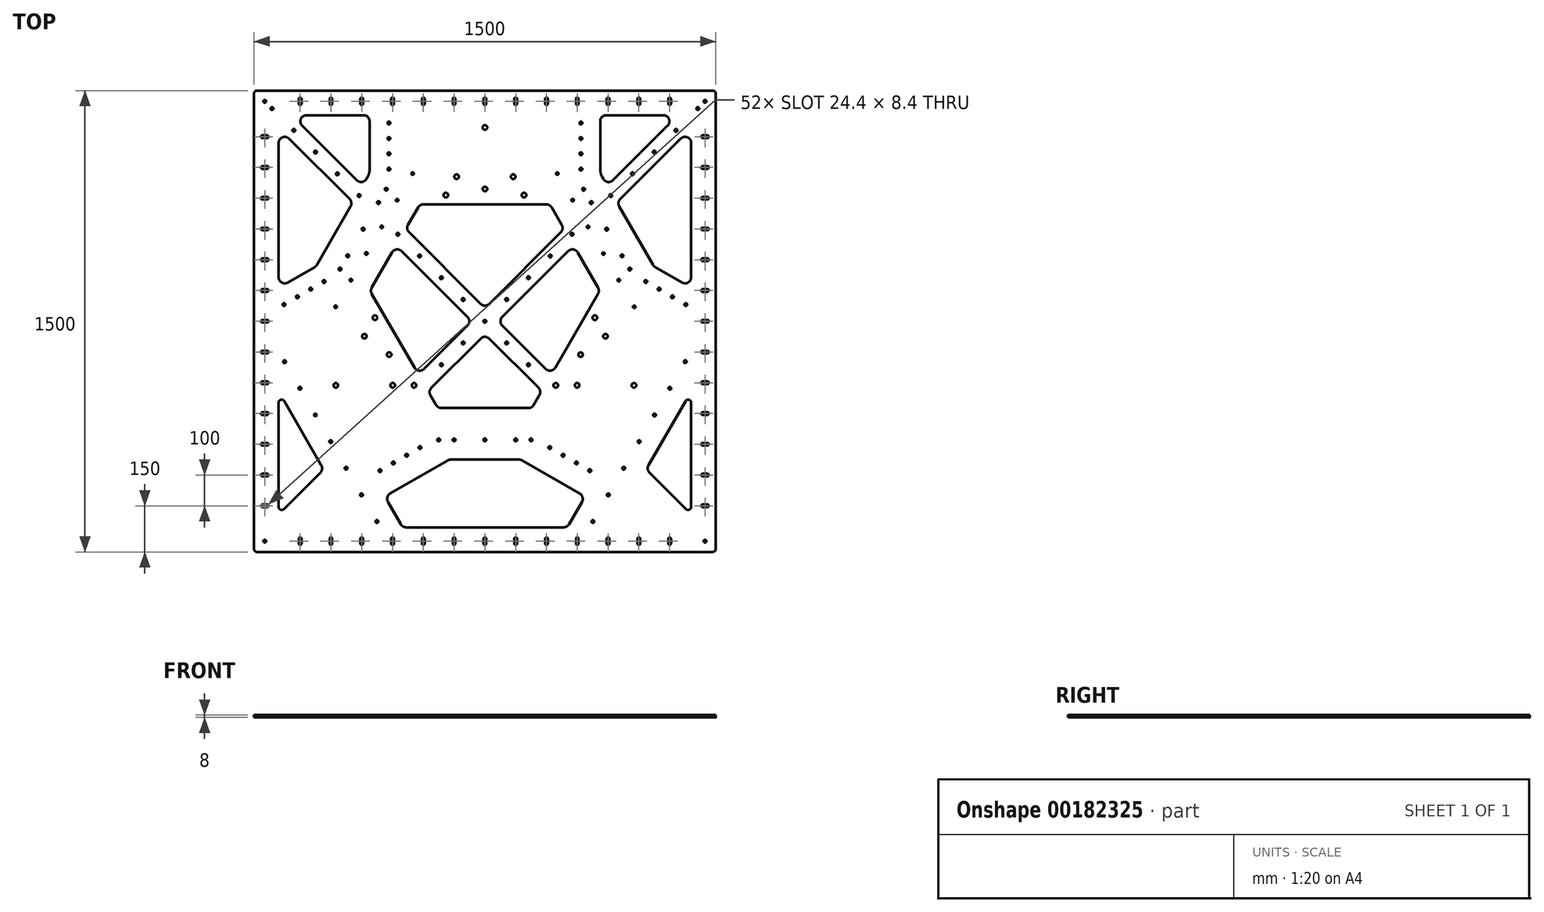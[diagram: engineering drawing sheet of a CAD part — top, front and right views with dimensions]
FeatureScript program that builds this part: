
annotation { "Feature Type Name" : "Feature", "Feature Type Description" : "" }
export const myFeature = defineFeature(function(context is Context, id is Id, definition is map)
    precondition{}
    {
        {
            var Q0;
            Q0=qCreatedBy(makeId("Top.planeOp"),FACE);
            var sketch = newSketch(context, id + "F0", { "sketchPlane" : qUnion([Q0])});
            skLineSegment(sketch, "E0.bottom", {"start": v(750, -750) * mm, "end": v(-750, -750) * mm});
            skLineSegment(sketch, "E0.top", {"start": v(750, 750) * mm, "end": v(-750, 750) * mm});
            skLineSegment(sketch, "E0.left", {"start": v(750, -750) * mm, "end": v(750, 750) * mm});
            skLineSegment(sketch, "E0.right", {"start": v(-750, -750) * mm, "end": v(-750, 750) * mm});
            skPoint(sketch, "E0.middle", {"position": v(0, 0) * mm});
            skSolve(sketch);
        }
        {
            var Q0;
            Q0=qSketchRegion(id+"F0",true);
            extrude(context, id + "F1", {"entities" : qUnion([Q0]), "depth" : 8 * mm});
        }
        {
            var Q0;
            Q0=makeQuery(id+"F1.opExtrude","CAP_FACE",FACE,{"disambiguationData":[OSD([sQuery(id+"F0.wireOp",EDGE,"E0.bottom"),sQuery(id+"F0.wireOp",EDGE,"E0.top"),sQuery(id+"F0.wireOp",EDGE,"E0.left"),sQuery(id+"F0.wireOp",EDGE,"E0.right")])],"isStart":false});
            var sketch = newSketch(context, id + "F2", { "sketchPlane" : qUnion([Q0])});
            skLineSegment(sketch, "E1", {"start": v(0, -750) * mm, "end": v(0, 750) * mm, "construction": true});
            skCircle(sketch, "E2", {"center": v(0, 71) * mm, "radius": 559 * mm, "construction": true});
            skCircle(sketch, "E3", {"center": v(0, 630) * mm, "radius": 7.5 * mm});
            skLineSegment(sketch, "E4", {"start": v(0, 71) * mm, "end": v(-275.24, -87.91) * mm, "construction": true});
            skLineSegment(sketch, "E5", {"start": v(0, 71) * mm, "end": v(329.13, -119.03) * mm, "construction": true});
            skCircle(sketch, "E6.MirrorC", {"center": v(-484.1, -208.5) * mm, "radius": 7.5 * mm});
            skCircle(sketch, "E7.MirrorC", {"center": v(484.1, -208.5) * mm, "radius": 7.5 * mm});
            skCircle(sketch, "E8", {"center": v(0, 71) * mm, "radius": 362 * mm, "construction": true});
            skCircle(sketch, "E9", {"center": v(0, 71) * mm, "radius": 409.5 * mm, "construction": true});
            skCircle(sketch, "E10", {"center": v(-92, 470.03) * mm, "radius": 7.5 * mm});
            skCircle(sketch, "E11.MirrorC", {"center": v(92, 470.03) * mm, "radius": 7.5 * mm});
            skCircle(sketch, "E12", {"center": v(-127, 410) * mm, "radius": 7.5 * mm});
            skCircle(sketch, "E13.MirrorC", {"center": v(127, 410) * mm, "radius": 7.5 * mm});
            skCircle(sketch, "E14.MirrorC", {"center": v(-230.07, -208.48) * mm, "radius": 7.5 * mm});
            skCircle(sketch, "E15.MirrorC", {"center": v(-357.07, 11.49) * mm, "radius": 7.5 * mm});
            skCircle(sketch, "E16.MirrorC", {"center": v(-299.57, -208.2) * mm, "radius": 7.5 * mm});
            skCircle(sketch, "E17.MirrorC", {"center": v(-391.57, -48.84) * mm, "radius": 7.5 * mm});
            skCircle(sketch, "E18.MirrorC", {"center": v(391.57, -48.84) * mm, "radius": 7.5 * mm});
            skCircle(sketch, "E19.MirrorC", {"center": v(299.57, -208.2) * mm, "radius": 7.5 * mm});
            skCircle(sketch, "E20.MirrorC", {"center": v(230.07, -208.48) * mm, "radius": 7.5 * mm});
            skCircle(sketch, "E21.MirrorC", {"center": v(357.07, 11.49) * mm, "radius": 7.5 * mm});
            skPoint(sketch, "E22.middle", {"position": v(0, 435.08) * mm});
            skCircle(sketch, "E23", {"center": v(0, 430) * mm, "radius": 7.5 * mm});
            skCircle(sketch, "E24.MirrorC", {"center": v(310.9, -108.5) * mm, "radius": 7.5 * mm});
            skCircle(sketch, "E25.MirrorC", {"center": v(-310.9, -108.5) * mm, "radius": 7.5 * mm});
            skSolve(sketch);
        }
        {
            var Q0;
            Q0=qSketchRegion(id+"F2",true);
            extrude(context, id + "F3", {"entities" : qUnion([Q0]), "operationType" : NewBodyOperationType.REMOVE, "endBound" : BoundingType.THROUGH_ALL, "oppositeDirection" : true, "depth" : 25 * mm});
        }
        {
            var Q0;
            Q0=makeQuery(id+"F1.opExtrude","CAP_FACE",FACE,{"disambiguationData":[OSD([sQuery(id+"F0.wireOp",EDGE,"E0.bottom"),sQuery(id+"F0.wireOp",EDGE,"E0.top"),sQuery(id+"F0.wireOp",EDGE,"E0.left"),sQuery(id+"F0.wireOp",EDGE,"E0.right")])],"isStart":false});
            var sketch = newSketch(context, id + "F4", { "sketchPlane" : qUnion([Q0])});
            skLineSegment(sketch, "E26", {"start": v(0, 750) * mm, "end": v(0, -750) * mm, "construction": true});
            skLineSegment(sketch, "E27", {"start": v(-627.57, 670) * mm, "end": v(-374.68, 670) * mm});
            skLineSegment(sketch, "E28", {"start": v(-397.7, 440.12) * mm, "end": v(-627.57, 670) * mm});
            skLineSegment(sketch, "E29.MirrorCS", {"start": v(627.57, 670) * mm, "end": v(374.68, 670) * mm});
            skLineSegment(sketch, "E30.MirrorCS", {"start": v(397.7, 440.12) * mm, "end": v(627.57, 670) * mm});
            skLineSegment(sketch, "E31", {"start": v(-257.5, 299.93) * mm, "end": v(257.5, 299.93) * mm, "construction": true});
            skLineSegment(sketch, "E32", {"start": v(257.5, 299.93) * mm, "end": v(0, 42.43) * mm});
            skLineSegment(sketch, "E33.MirrorCS", {"start": v(-257.5, 299.93) * mm, "end": v(0, 42.43) * mm});
            skLineSegment(sketch, "E34", {"start": v(-399.35, 0) * mm, "end": v(437.87, 0) * mm, "construction": true});
            skLineSegment(sketch, "E35.MirrorCS", {"start": v(-257.5, -299.93) * mm, "end": v(0, -42.43) * mm});
            skLineSegment(sketch, "E36.MirrorCS", {"start": v(-257.5, -299.93) * mm, "end": v(257.5, -299.93) * mm, "construction": true});
            skLineSegment(sketch, "E37.MirrorCS", {"start": v(257.5, -299.93) * mm, "end": v(0, -42.43) * mm});
            skLineSegment(sketch, "E38", {"start": v(-215.67, -173.24) * mm, "end": v(-42.43, 0) * mm});
            skLineSegment(sketch, "E39.MirrorCS", {"start": v(-215.67, 173.24) * mm, "end": v(-42.43, 0) * mm});
            skLineSegment(sketch, "E40.MirrorCS", {"start": v(215.67, 173.24) * mm, "end": v(42.43, 0) * mm});
            skLineSegment(sketch, "E41.MirrorCS", {"start": v(215.67, -173.24) * mm, "end": v(42.43, 0) * mm});
            skLineSegment(sketch, "E42", {"start": v(750, 750) * mm, "end": v(-750, -750) * mm, "construction": true});
            skLineSegment(sketch, "E43", {"start": v(-750, 750) * mm, "end": v(750, -750) * mm, "construction": true});
            skLineSegment(sketch, "E44", {"start": v(-750, -707.57) * mm, "end": v(707.57, 750) * mm, "construction": true});
            skLineSegment(sketch, "E45", {"start": v(750, 707.57) * mm, "end": v(-707.57, -750) * mm, "construction": true});
            skLineSegment(sketch, "E46", {"start": v(-215.67, 173.24) * mm, "end": v(-315.69, 0) * mm, "construction": true});
            skLineSegment(sketch, "E47", {"start": v(-315.69, 0) * mm, "end": v(-215.67, -173.24) * mm});
            skLineSegment(sketch, "E48.MirrorCS", {"start": v(315.69, 0) * mm, "end": v(215.67, -173.24) * mm});
            skLineSegment(sketch, "E49.MirrorCS", {"start": v(215.67, 173.24) * mm, "end": v(315.69, 0) * mm, "construction": true});
            skLineSegment(sketch, "E50", {"start": v(670, 627.57) * mm, "end": v(428.76, 386.33) * mm});
            skLineSegment(sketch, "E51", {"start": v(670, 108.48) * mm, "end": v(670, 627.57) * mm});
            skLineSegment(sketch, "E52", {"start": v(-184.6, -227.04) * mm, "end": v(-257.5, -299.93) * mm});
            skLineSegment(sketch, "E53", {"start": v(-184.6, -227.04) * mm, "end": v(184.6, -227.04) * mm, "construction": true});
            skLineSegment(sketch, "E54", {"start": v(257.5, -299.93) * mm, "end": v(184.6, -227.04) * mm});
            skLineSegment(sketch, "E55", {"start": v(-670, -227.57) * mm, "end": v(-670, -627.57) * mm});
            skLineSegment(sketch, "E56", {"start": v(-670, -627.57) * mm, "end": v(-523.59, -481.16) * mm});
            skLineSegment(sketch, "E57", {"start": v(-523.59, -481.16) * mm, "end": v(-670, -227.57) * mm});
            skLineSegment(sketch, "E58.MirrorCS", {"start": v(523.59, -481.16) * mm, "end": v(670, -227.57) * mm});
            skLineSegment(sketch, "E59.MirrorCS", {"start": v(670, -627.57) * mm, "end": v(523.59, -481.16) * mm});
            skLineSegment(sketch, "E60.MirrorCS", {"start": v(670, -227.57) * mm, "end": v(670, -627.57) * mm});
            skLineSegment(sketch, "E61", {"start": v(0, -450) * mm, "end": v(-117.15, -450) * mm});
            skLineSegment(sketch, "E62", {"start": v(-117.15, -450) * mm, "end": v(-325, -570) * mm});
            skLineSegment(sketch, "E63", {"start": v(-325, -570) * mm, "end": v(0, -570) * mm, "construction": true});
            skLineSegment(sketch, "E64.MirrorCS", {"start": v(0, -450) * mm, "end": v(117.15, -450) * mm});
            skLineSegment(sketch, "E65.MirrorCS", {"start": v(325, -570) * mm, "end": v(0, -570) * mm, "construction": true});
            skLineSegment(sketch, "E66.MirrorCS", {"start": v(117.15, -450) * mm, "end": v(325, -570) * mm});
            skLineSegment(sketch, "E67.MirrorCS", {"start": v(-670, 108.48) * mm, "end": v(-670, 627.57) * mm});
            skLineSegment(sketch, "E68.MirrorCS", {"start": v(-670, 627.57) * mm, "end": v(-428.76, 386.33) * mm});
            skLineSegment(sketch, "E69", {"start": v(428.76, 386.33) * mm, "end": v(548.76, 178.48) * mm});
            skLineSegment(sketch, "E70", {"start": v(548.76, 178.48) * mm, "end": v(670, 108.48) * mm});
            skLineSegment(sketch, "E71.MirrorCS", {"start": v(-428.76, 386.33) * mm, "end": v(-548.76, 178.48) * mm});
            skLineSegment(sketch, "E72.MirrorCS", {"start": v(-548.76, 178.48) * mm, "end": v(-670, 108.48) * mm});
            skLineSegment(sketch, "E73", {"start": v(-184.6, -227.04) * mm, "end": v(-152.63, -282.43) * mm});
            skLineSegment(sketch, "E74", {"start": v(-152.63, -282.43) * mm, "end": v(0, -282.43) * mm});
            skLineSegment(sketch, "E75.MirrorCS", {"start": v(152.63, -282.43) * mm, "end": v(0, -282.43) * mm});
            skLineSegment(sketch, "E76.MirrorCS", {"start": v(184.6, -227.04) * mm, "end": v(152.63, -282.43) * mm});
            skLineSegment(sketch, "E77", {"start": v(-408.03, 159.94) * mm, "end": v(-88.62, -393.3) * mm, "construction": true});
            skLineSegment(sketch, "E78", {"start": v(-215.67, 173.24) * mm, "end": v(-288.56, 246.13) * mm});
            skLineSegment(sketch, "E79", {"start": v(-288.56, 246.13) * mm, "end": v(-373.18, 99.57) * mm});
            skLineSegment(sketch, "E80", {"start": v(-315.69, 0) * mm, "end": v(-373.18, 99.57) * mm});
            skLineSegment(sketch, "E81.MirrorCS", {"start": v(288.56, 246.13) * mm, "end": v(373.18, 99.57) * mm});
            skLineSegment(sketch, "E82.MirrorCS", {"start": v(315.69, 0) * mm, "end": v(373.18, 99.57) * mm});
            skLineSegment(sketch, "E83.MirrorCS", {"start": v(215.67, 173.24) * mm, "end": v(288.56, 246.13) * mm});
            skLineSegment(sketch, "E84", {"start": v(-257.5, 299.93) * mm, "end": v(-462.8, -55.67) * mm, "construction": true});
            skLineSegment(sketch, "E85", {"start": v(-257.5, 299.93) * mm, "end": v(-211.31, 379.93) * mm});
            skLineSegment(sketch, "E86", {"start": v(-211.31, 379.93) * mm, "end": v(0, 379.93) * mm});
            skLineSegment(sketch, "E87.MirrorCS", {"start": v(211.31, 379.93) * mm, "end": v(0, 379.93) * mm});
            skLineSegment(sketch, "E88.MirrorCS", {"start": v(257.5, 299.93) * mm, "end": v(211.31, 379.93) * mm});
            skLineSegment(sketch, "E89", {"start": v(-325, -570) * mm, "end": v(-267.26, -670) * mm});
            skLineSegment(sketch, "E90", {"start": v(-267.26, -670) * mm, "end": v(0, -670) * mm});
            skLineSegment(sketch, "E91.MirrorCS", {"start": v(267.26, -670) * mm, "end": v(0, -670) * mm});
            skLineSegment(sketch, "E92.MirrorCS", {"start": v(325, -570) * mm, "end": v(267.26, -670) * mm});
            skLineSegment(sketch, "E93", {"start": v(428.76, 386.33) * mm, "end": v(397.7, 440.12) * mm, "construction": true});
            skLineSegment(sketch, "E94", {"start": v(397.7, 440.12) * mm, "end": v(374.68, 480) * mm});
            skLineSegment(sketch, "E95", {"start": v(374.68, 480) * mm, "end": v(374.68, 670) * mm});
            skLineSegment(sketch, "E96.MirrorCS", {"start": v(-374.68, 480) * mm, "end": v(-374.68, 670) * mm});
            skLineSegment(sketch, "E97.MirrorCS", {"start": v(-397.7, 440.12) * mm, "end": v(-374.68, 480) * mm});
            skSolve(sketch);
        }
        {
            var Q0;
            Q0 = qSketchRegion(id + "F4", true);
            extrude(context, id + "F5", {"entities" : qUnion([Q0]), "operationType" : NewBodyOperationType.REMOVE, "endBound" : BoundingType.THROUGH_ALL, "oppositeDirection" : true, "depth" : 25 * mm});
        }
        {
            var Q0;
            Q0=makeQuery(id+"F1.opExtrude","CAP_FACE",FACE,{"disambiguationData":[OSD([sQuery(id+"F0.wireOp",EDGE,"E0.bottom"),sQuery(id+"F0.wireOp",EDGE,"E0.top"),sQuery(id+"F0.wireOp",EDGE,"E0.left"),sQuery(id+"F0.wireOp",EDGE,"E0.right")])],"isStart":false});
            var sketch = newSketch(context, id + "F6", { "sketchPlane" : qUnion([Q0])});
            skLineSegment(sketch, "E98", {"start": v(0, 750) * mm, "end": v(0, -750) * mm, "construction": true});
            skLineSegment(sketch, "E99.left", {"start": v(-595.8, 707) * mm, "end": v(-595.8, 723) * mm});
            skLineSegment(sketch, "E99.right", {"start": v(-604.2, 707) * mm, "end": v(-604.2, 723) * mm});
            skPoint(sketch, "E99.middle", {"position": v(-600, 715) * mm});
            skArc(sketch, "E100", {"start": v(-595.8, 723) * mm, "mid": v(-600, 727.2) * mm, "end": v(-604.2, 723) * mm});
            skArc(sketch, "E101", {"start": v(-604.2, 707) * mm, "mid": v(-600, 702.8) * mm, "end": v(-595.8, 707) * mm});
            skLineSegment(sketch, "E102", {"start": v(-604.2, 723) * mm, "end": v(-595.8, 723) * mm, "construction": true});
            skArc(sketch, "E103.1.0.0", {"start": v(-504.2, 707) * mm, "mid": v(-500, 702.8) * mm, "end": v(-495.8, 707) * mm});
            skLineSegment(sketch, "E103.1.0.1", {"start": v(-495.8, 707) * mm, "end": v(-495.8, 723) * mm});
            skArc(sketch, "E103.1.0.2", {"start": v(-495.8, 723) * mm, "mid": v(-500, 727.2) * mm, "end": v(-504.2, 723) * mm});
            skLineSegment(sketch, "E103.1.0.3", {"start": v(-504.2, 707) * mm, "end": v(-504.2, 723) * mm});
            skArc(sketch, "E103.2.0.0", {"start": v(-404.2, 707) * mm, "mid": v(-400, 702.8) * mm, "end": v(-395.8, 707) * mm});
            skLineSegment(sketch, "E103.2.0.1", {"start": v(-395.8, 707) * mm, "end": v(-395.8, 723) * mm});
            skArc(sketch, "E103.2.0.2", {"start": v(-395.8, 723) * mm, "mid": v(-400, 727.2) * mm, "end": v(-404.2, 723) * mm});
            skLineSegment(sketch, "E103.2.0.3", {"start": v(-404.2, 707) * mm, "end": v(-404.2, 723) * mm});
            skArc(sketch, "E103.3.0.0", {"start": v(-304.2, 707) * mm, "mid": v(-300, 702.8) * mm, "end": v(-295.8, 707) * mm});
            skLineSegment(sketch, "E103.3.0.1", {"start": v(-295.8, 707) * mm, "end": v(-295.8, 723) * mm});
            skArc(sketch, "E103.3.0.2", {"start": v(-295.8, 723) * mm, "mid": v(-300, 727.2) * mm, "end": v(-304.2, 723) * mm});
            skLineSegment(sketch, "E103.3.0.3", {"start": v(-304.2, 707) * mm, "end": v(-304.2, 723) * mm});
            skArc(sketch, "E103.4.0.0", {"start": v(-204.2, 707) * mm, "mid": v(-200, 702.8) * mm, "end": v(-195.8, 707) * mm});
            skLineSegment(sketch, "E103.4.0.1", {"start": v(-195.8, 707) * mm, "end": v(-195.8, 723) * mm});
            skArc(sketch, "E103.4.0.2", {"start": v(-195.8, 723) * mm, "mid": v(-200, 727.2) * mm, "end": v(-204.2, 723) * mm});
            skLineSegment(sketch, "E103.4.0.3", {"start": v(-204.2, 707) * mm, "end": v(-204.2, 723) * mm});
            skArc(sketch, "E103.5.0.0", {"start": v(-104.2, 707) * mm, "mid": v(-100, 702.8) * mm, "end": v(-95.8, 707) * mm});
            skLineSegment(sketch, "E103.5.0.1", {"start": v(-95.8, 707) * mm, "end": v(-95.8, 723) * mm});
            skArc(sketch, "E103.5.0.2", {"start": v(-95.8, 723) * mm, "mid": v(-100, 727.2) * mm, "end": v(-104.2, 723) * mm});
            skLineSegment(sketch, "E103.5.0.3", {"start": v(-104.2, 707) * mm, "end": v(-104.2, 723) * mm});
            skArc(sketch, "E103.6.0.0", {"start": v(-4.2, 707) * mm, "mid": v(0, 702.8) * mm, "end": v(4.2, 707) * mm});
            skLineSegment(sketch, "E103.6.0.1", {"start": v(4.2, 707) * mm, "end": v(4.2, 723) * mm});
            skArc(sketch, "E103.6.0.2", {"start": v(4.2, 723) * mm, "mid": v(0, 727.2) * mm, "end": v(-4.2, 723) * mm});
            skLineSegment(sketch, "E103.6.0.3", {"start": v(-4.2, 707) * mm, "end": v(-4.2, 723) * mm});
            skArc(sketch, "E103.7.0.0", {"start": v(95.8, 707) * mm, "mid": v(100, 702.8) * mm, "end": v(104.2, 707) * mm});
            skLineSegment(sketch, "E103.7.0.1", {"start": v(104.2, 707) * mm, "end": v(104.2, 723) * mm});
            skArc(sketch, "E103.7.0.2", {"start": v(104.2, 723) * mm, "mid": v(100, 727.2) * mm, "end": v(95.8, 723) * mm});
            skLineSegment(sketch, "E103.7.0.3", {"start": v(95.8, 707) * mm, "end": v(95.8, 723) * mm});
            skArc(sketch, "E103.8.0.0", {"start": v(195.8, 707) * mm, "mid": v(200, 702.8) * mm, "end": v(204.2, 707) * mm});
            skLineSegment(sketch, "E103.8.0.1", {"start": v(204.2, 707) * mm, "end": v(204.2, 723) * mm});
            skArc(sketch, "E103.8.0.2", {"start": v(204.2, 723) * mm, "mid": v(200, 727.2) * mm, "end": v(195.8, 723) * mm});
            skLineSegment(sketch, "E103.8.0.3", {"start": v(195.8, 707) * mm, "end": v(195.8, 723) * mm});
            skArc(sketch, "E103.9.0.0", {"start": v(295.8, 707) * mm, "mid": v(300, 702.8) * mm, "end": v(304.2, 707) * mm});
            skLineSegment(sketch, "E103.9.0.1", {"start": v(304.2, 707) * mm, "end": v(304.2, 723) * mm});
            skArc(sketch, "E103.9.0.2", {"start": v(304.2, 723) * mm, "mid": v(300, 727.2) * mm, "end": v(295.8, 723) * mm});
            skLineSegment(sketch, "E103.9.0.3", {"start": v(295.8, 707) * mm, "end": v(295.8, 723) * mm});
            skArc(sketch, "E103.10.0.0", {"start": v(395.8, 707) * mm, "mid": v(400, 702.8) * mm, "end": v(404.2, 707) * mm});
            skLineSegment(sketch, "E103.10.0.1", {"start": v(404.2, 707) * mm, "end": v(404.2, 723) * mm});
            skArc(sketch, "E103.10.0.2", {"start": v(404.2, 723) * mm, "mid": v(400, 727.2) * mm, "end": v(395.8, 723) * mm});
            skLineSegment(sketch, "E103.10.0.3", {"start": v(395.8, 707) * mm, "end": v(395.8, 723) * mm});
            skArc(sketch, "E103.11.0.0", {"start": v(495.8, 707) * mm, "mid": v(500, 702.8) * mm, "end": v(504.2, 707) * mm});
            skLineSegment(sketch, "E103.11.0.1", {"start": v(504.2, 707) * mm, "end": v(504.2, 723) * mm});
            skArc(sketch, "E103.11.0.2", {"start": v(504.2, 723) * mm, "mid": v(500, 727.2) * mm, "end": v(495.8, 723) * mm});
            skLineSegment(sketch, "E103.11.0.3", {"start": v(495.8, 707) * mm, "end": v(495.8, 723) * mm});
            skArc(sketch, "E103.12.0.0", {"start": v(595.8, 707) * mm, "mid": v(600, 702.8) * mm, "end": v(604.2, 707) * mm});
            skLineSegment(sketch, "E103.12.0.1", {"start": v(604.2, 707) * mm, "end": v(604.2, 723) * mm});
            skArc(sketch, "E103.12.0.2", {"start": v(604.2, 723) * mm, "mid": v(600, 727.2) * mm, "end": v(595.8, 723) * mm});
            skLineSegment(sketch, "E103.12.0.3", {"start": v(595.8, 707) * mm, "end": v(595.8, 723) * mm});
            skLineSegment(sketch, "E103.direction1", {"start": v(-604.2, 707) * mm, "end": v(-504.2, 707) * mm, "construction": true});
            skLineSegment(sketch, "E104", {"start": v(-750, 723) * mm, "end": v(750, 723) * mm, "construction": true});
            skLineSegment(sketch, "E105", {"start": v(-750, 0) * mm, "end": v(750, 0) * mm, "construction": true});
            skArc(sketch, "E106.MirrorCS", {"start": v(-295.8, -723) * mm, "mid": v(-300, -727.2) * mm, "end": v(-304.2, -723) * mm});
            skArc(sketch, "E107.MirrorCS", {"start": v(-495.8, -723) * mm, "mid": v(-500, -727.2) * mm, "end": v(-504.2, -723) * mm});
            skLineSegment(sketch, "E108.MirrorCS", {"start": v(304.2, -707) * mm, "end": v(304.2, -723) * mm});
            skLineSegment(sketch, "E109.MirrorCS", {"start": v(-495.8, -707) * mm, "end": v(-495.8, -723) * mm});
            skArc(sketch, "E110.MirrorCS", {"start": v(-504.2, -707) * mm, "mid": v(-500, -702.8) * mm, "end": v(-495.8, -707) * mm});
            skLineSegment(sketch, "E111.MirrorCS", {"start": v(-604.2, -723) * mm, "end": v(-595.8, -723) * mm, "construction": true});
            skArc(sketch, "E112.MirrorCS", {"start": v(-604.2, -707) * mm, "mid": v(-600, -702.8) * mm, "end": v(-595.8, -707) * mm});
            skArc(sketch, "E113.MirrorCS", {"start": v(-595.8, -723) * mm, "mid": v(-600, -727.2) * mm, "end": v(-604.2, -723) * mm});
            skLineSegment(sketch, "E114.MirrorCS", {"start": v(-604.2, -707) * mm, "end": v(-604.2, -723) * mm});
            skLineSegment(sketch, "E115.MirrorCS", {"start": v(-295.8, -707) * mm, "end": v(-295.8, -723) * mm});
            skLineSegment(sketch, "E116.MirrorCS", {"start": v(-595.8, -707) * mm, "end": v(-595.8, -723) * mm});
            skArc(sketch, "E117.MirrorCS", {"start": v(-304.2, -707) * mm, "mid": v(-300, -702.8) * mm, "end": v(-295.8, -707) * mm});
            skLineSegment(sketch, "E118.MirrorCS", {"start": v(-304.2, -707) * mm, "end": v(-304.2, -723) * mm});
            skArc(sketch, "E119.MirrorCS", {"start": v(295.8, -707) * mm, "mid": v(300, -702.8) * mm, "end": v(304.2, -707) * mm});
            skArc(sketch, "E120.MirrorCS", {"start": v(304.2, -723) * mm, "mid": v(300, -727.2) * mm, "end": v(295.8, -723) * mm});
            skLineSegment(sketch, "E121.MirrorCS", {"start": v(295.8, -707) * mm, "end": v(295.8, -723) * mm});
            skLineSegment(sketch, "E122.MirrorCS", {"start": v(-504.2, -707) * mm, "end": v(-504.2, -723) * mm});
            skArc(sketch, "E123.MirrorCS", {"start": v(-4.2, -707) * mm, "mid": v(0, -702.8) * mm, "end": v(4.2, -707) * mm});
            skArc(sketch, "E124.MirrorCS", {"start": v(104.2, -723) * mm, "mid": v(100, -727.2) * mm, "end": v(95.8, -723) * mm});
            skLineSegment(sketch, "E125.MirrorCS", {"start": v(-4.2, -707) * mm, "end": v(-4.2, -723) * mm});
            skArc(sketch, "E126.MirrorCS", {"start": v(4.2, -723) * mm, "mid": v(0, -727.2) * mm, "end": v(-4.2, -723) * mm});
            skLineSegment(sketch, "E127.MirrorCS", {"start": v(4.2, -707) * mm, "end": v(4.2, -723) * mm});
            skArc(sketch, "E128.MirrorCS", {"start": v(-195.8, -723) * mm, "mid": v(-200, -727.2) * mm, "end": v(-204.2, -723) * mm});
            skLineSegment(sketch, "E129.MirrorCS", {"start": v(395.8, -707) * mm, "end": v(395.8, -723) * mm});
            skArc(sketch, "E130.MirrorCS", {"start": v(504.2, -723) * mm, "mid": v(500, -727.2) * mm, "end": v(495.8, -723) * mm});
            skLineSegment(sketch, "E131.MirrorCS", {"start": v(-395.8, -707) * mm, "end": v(-395.8, -723) * mm});
            skArc(sketch, "E132.MirrorCS", {"start": v(395.8, -707) * mm, "mid": v(400, -702.8) * mm, "end": v(404.2, -707) * mm});
            skArc(sketch, "E133.MirrorCS", {"start": v(604.2, -723) * mm, "mid": v(600, -727.2) * mm, "end": v(595.8, -723) * mm});
            skLineSegment(sketch, "E134.MirrorCS", {"start": v(204.2, -707) * mm, "end": v(204.2, -723) * mm});
            skLineSegment(sketch, "E135.MirrorCS", {"start": v(-195.8, -707) * mm, "end": v(-195.8, -723) * mm});
            skArc(sketch, "E136.MirrorCS", {"start": v(-404.2, -707) * mm, "mid": v(-400, -702.8) * mm, "end": v(-395.8, -707) * mm});
            skLineSegment(sketch, "E137.MirrorCS", {"start": v(-95.8, -707) * mm, "end": v(-95.8, -723) * mm});
            skLineSegment(sketch, "E138.MirrorCS", {"start": v(495.8, -707) * mm, "end": v(495.8, -723) * mm});
            skLineSegment(sketch, "E139.MirrorCS", {"start": v(95.8, -707) * mm, "end": v(95.8, -723) * mm});
            skLineSegment(sketch, "E140.MirrorCS", {"start": v(-404.2, -707) * mm, "end": v(-404.2, -723) * mm});
            skLineSegment(sketch, "E141.MirrorCS", {"start": v(504.2, -707) * mm, "end": v(504.2, -723) * mm});
            skArc(sketch, "E142.MirrorCS", {"start": v(-104.2, -707) * mm, "mid": v(-100, -702.8) * mm, "end": v(-95.8, -707) * mm});
            skLineSegment(sketch, "E143.MirrorCS", {"start": v(104.2, -707) * mm, "end": v(104.2, -723) * mm});
            skArc(sketch, "E144.MirrorCS", {"start": v(-395.8, -723) * mm, "mid": v(-400, -727.2) * mm, "end": v(-404.2, -723) * mm});
            skArc(sketch, "E145.MirrorCS", {"start": v(-95.8, -723) * mm, "mid": v(-100, -727.2) * mm, "end": v(-104.2, -723) * mm});
            skLineSegment(sketch, "E146.MirrorCS", {"start": v(604.2, -707) * mm, "end": v(604.2, -723) * mm});
            skArc(sketch, "E147.MirrorCS", {"start": v(595.8, -707) * mm, "mid": v(600, -702.8) * mm, "end": v(604.2, -707) * mm});
            skLineSegment(sketch, "E148.MirrorCS", {"start": v(-104.2, -707) * mm, "end": v(-104.2, -723) * mm});
            skLineSegment(sketch, "E149.MirrorCS", {"start": v(595.8, -707) * mm, "end": v(595.8, -723) * mm});
            skArc(sketch, "E150.MirrorCS", {"start": v(495.8, -707) * mm, "mid": v(500, -702.8) * mm, "end": v(504.2, -707) * mm});
            skArc(sketch, "E151.MirrorCS", {"start": v(195.8, -707) * mm, "mid": v(200, -702.8) * mm, "end": v(204.2, -707) * mm});
            skArc(sketch, "E152.MirrorCS", {"start": v(95.8, -707) * mm, "mid": v(100, -702.8) * mm, "end": v(104.2, -707) * mm});
            skArc(sketch, "E153.MirrorCS", {"start": v(204.2, -723) * mm, "mid": v(200, -727.2) * mm, "end": v(195.8, -723) * mm});
            skLineSegment(sketch, "E154.MirrorCS", {"start": v(-204.2, -707) * mm, "end": v(-204.2, -723) * mm});
            skLineSegment(sketch, "E155.MirrorCS", {"start": v(195.8, -707) * mm, "end": v(195.8, -723) * mm});
            skArc(sketch, "E156.MirrorCS", {"start": v(404.2, -723) * mm, "mid": v(400, -727.2) * mm, "end": v(395.8, -723) * mm});
            skLineSegment(sketch, "E157.MirrorCS", {"start": v(404.2, -707) * mm, "end": v(404.2, -723) * mm});
            skArc(sketch, "E158.MirrorCS", {"start": v(-204.2, -707) * mm, "mid": v(-200, -702.8) * mm, "end": v(-195.8, -707) * mm});
            skLineSegment(sketch, "E159.MirrorCS", {"start": v(-604.2, -707) * mm, "end": v(-504.2, -707) * mm, "construction": true});
            skPoint(sketch, "E160.MirrorP", {"position": v(-600, -715) * mm});
            skLineSegment(sketch, "E161", {"start": v(-750, 750) * mm, "end": v(750, -750) * mm, "construction": true});
            skLineSegment(sketch, "E162.MirrorCS", {"start": v(-707, 595.8) * mm, "end": v(-723, 595.8) * mm});
            skLineSegment(sketch, "E163.MirrorCS", {"start": v(-707, 604.2) * mm, "end": v(-723, 604.2) * mm});
            skArc(sketch, "E164.MirrorCS", {"start": v(-723, 595.8) * mm, "mid": v(-727.2, 600) * mm, "end": v(-723, 604.2) * mm});
            skArc(sketch, "E165.MirrorCS", {"start": v(-707, 604.2) * mm, "mid": v(-702.8, 600) * mm, "end": v(-707, 595.8) * mm});
            skLineSegment(sketch, "E166.MirrorCS", {"start": v(-723, 604.2) * mm, "end": v(-723, 595.8) * mm, "construction": true});
            skArc(sketch, "E167.MirrorCS", {"start": v(-723, 495.8) * mm, "mid": v(-727.2, 500) * mm, "end": v(-723, 504.2) * mm});
            skArc(sketch, "E168.MirrorCS", {"start": v(-723, -104.2) * mm, "mid": v(-727.2, -100) * mm, "end": v(-723, -95.8) * mm});
            skLineSegment(sketch, "E169.MirrorCS", {"start": v(-707, 504.2) * mm, "end": v(-723, 504.2) * mm});
            skArc(sketch, "E170.MirrorCS", {"start": v(-723, 295.8) * mm, "mid": v(-727.2, 300) * mm, "end": v(-723, 304.2) * mm});
            skArc(sketch, "E171.MirrorCS", {"start": v(-707, 404.2) * mm, "mid": v(-702.8, 400) * mm, "end": v(-707, 395.8) * mm});
            skArc(sketch, "E172.MirrorCS", {"start": v(-723, -504.2) * mm, "mid": v(-727.2, -500) * mm, "end": v(-723, -495.8) * mm});
            skLineSegment(sketch, "E173.MirrorCS", {"start": v(-707, 395.8) * mm, "end": v(-723, 395.8) * mm});
            skArc(sketch, "E174.MirrorCS", {"start": v(-723, 395.8) * mm, "mid": v(-727.2, 400) * mm, "end": v(-723, 404.2) * mm});
            skLineSegment(sketch, "E175.MirrorCS", {"start": v(-707, -95.8) * mm, "end": v(-723, -95.8) * mm});
            skLineSegment(sketch, "E176.MirrorCS", {"start": v(-707, 304.2) * mm, "end": v(-723, 304.2) * mm});
            skLineSegment(sketch, "E177.MirrorCS", {"start": v(-707, -495.8) * mm, "end": v(-723, -495.8) * mm});
            skArc(sketch, "E178.MirrorCS", {"start": v(-707, -595.8) * mm, "mid": v(-702.8, -600) * mm, "end": v(-707, -604.2) * mm});
            skArc(sketch, "E179.MirrorCS", {"start": v(-707, -195.8) * mm, "mid": v(-702.8, -200) * mm, "end": v(-707, -204.2) * mm});
            skArc(sketch, "E180.MirrorCS", {"start": v(-707, 204.2) * mm, "mid": v(-702.8, 200) * mm, "end": v(-707, 195.8) * mm});
            skLineSegment(sketch, "E181.MirrorCS", {"start": v(-707, -204.2) * mm, "end": v(-723, -204.2) * mm});
            skLineSegment(sketch, "E182.MirrorCS", {"start": v(-707, 195.8) * mm, "end": v(-723, 195.8) * mm});
            skLineSegment(sketch, "E183.MirrorCS", {"start": v(-707, -604.2) * mm, "end": v(-723, -604.2) * mm});
            skArc(sketch, "E184.MirrorCS", {"start": v(-723, -204.2) * mm, "mid": v(-727.2, -200) * mm, "end": v(-723, -195.8) * mm});
            skArc(sketch, "E185.MirrorCS", {"start": v(-723, 195.8) * mm, "mid": v(-727.2, 200) * mm, "end": v(-723, 204.2) * mm});
            skArc(sketch, "E186.MirrorCS", {"start": v(-723, -604.2) * mm, "mid": v(-727.2, -600) * mm, "end": v(-723, -595.8) * mm});
            skLineSegment(sketch, "E187.MirrorCS", {"start": v(-707, -195.8) * mm, "end": v(-723, -195.8) * mm});
            skLineSegment(sketch, "E188.MirrorCS", {"start": v(-707, 204.2) * mm, "end": v(-723, 204.2) * mm});
            skLineSegment(sketch, "E189.MirrorCS", {"start": v(-707, -595.8) * mm, "end": v(-723, -595.8) * mm});
            skArc(sketch, "E190.MirrorCS", {"start": v(-707, -295.8) * mm, "mid": v(-702.8, -300) * mm, "end": v(-707, -304.2) * mm});
            skArc(sketch, "E191.MirrorCS", {"start": v(-707, 104.2) * mm, "mid": v(-702.8, 100) * mm, "end": v(-707, 95.8) * mm});
            skLineSegment(sketch, "E192.MirrorCS", {"start": v(-707, -304.2) * mm, "end": v(-723, -304.2) * mm});
            skLineSegment(sketch, "E193.MirrorCS", {"start": v(-707, 95.8) * mm, "end": v(-723, 95.8) * mm});
            skArc(sketch, "E194.MirrorCS", {"start": v(-723, -304.2) * mm, "mid": v(-727.2, -300) * mm, "end": v(-723, -295.8) * mm});
            skArc(sketch, "E195.MirrorCS", {"start": v(-723, 95.8) * mm, "mid": v(-727.2, 100) * mm, "end": v(-723, 104.2) * mm});
            skLineSegment(sketch, "E196.MirrorCS", {"start": v(-707, -295.8) * mm, "end": v(-723, -295.8) * mm});
            skLineSegment(sketch, "E197.MirrorCS", {"start": v(-707, 104.2) * mm, "end": v(-723, 104.2) * mm});
            skArc(sketch, "E198.MirrorCS", {"start": v(-707, -395.8) * mm, "mid": v(-702.8, -400) * mm, "end": v(-707, -404.2) * mm});
            skArc(sketch, "E199.MirrorCS", {"start": v(-707, 4.2) * mm, "mid": v(-702.8, 0) * mm, "end": v(-707, -4.2) * mm});
            skLineSegment(sketch, "E200.MirrorCS", {"start": v(-707, -404.2) * mm, "end": v(-723, -404.2) * mm});
            skLineSegment(sketch, "E201.MirrorCS", {"start": v(-707, -4.2) * mm, "end": v(-723, -4.2) * mm});
            skLineSegment(sketch, "E202.MirrorCS", {"start": v(-707, 4.2) * mm, "end": v(-723, 4.2) * mm});
            skLineSegment(sketch, "E203.MirrorCS", {"start": v(-707, -395.8) * mm, "end": v(-723, -395.8) * mm});
            skArc(sketch, "E204.MirrorCS", {"start": v(-723, -404.2) * mm, "mid": v(-727.2, -400) * mm, "end": v(-723, -395.8) * mm});
            skArc(sketch, "E205.MirrorCS", {"start": v(-723, -4.2) * mm, "mid": v(-727.2, 0) * mm, "end": v(-723, 4.2) * mm});
            skArc(sketch, "E206.MirrorCS", {"start": v(-707, -95.8) * mm, "mid": v(-702.8, -100) * mm, "end": v(-707, -104.2) * mm});
            skArc(sketch, "E207.MirrorCS", {"start": v(-707, -495.8) * mm, "mid": v(-702.8, -500) * mm, "end": v(-707, -504.2) * mm});
            skLineSegment(sketch, "E208.MirrorCS", {"start": v(-707, -104.2) * mm, "end": v(-723, -104.2) * mm});
            skLineSegment(sketch, "E209.MirrorCS", {"start": v(-707, -504.2) * mm, "end": v(-723, -504.2) * mm});
            skLineSegment(sketch, "E210.MirrorCS", {"start": v(-707, 404.2) * mm, "end": v(-723, 404.2) * mm});
            skArc(sketch, "E211.MirrorCS", {"start": v(-707, 304.2) * mm, "mid": v(-702.8, 300) * mm, "end": v(-707, 295.8) * mm});
            skLineSegment(sketch, "E212.MirrorCS", {"start": v(-707, 295.8) * mm, "end": v(-723, 295.8) * mm});
            skArc(sketch, "E213.MirrorCS", {"start": v(-707, 504.2) * mm, "mid": v(-702.8, 500) * mm, "end": v(-707, 495.8) * mm});
            skLineSegment(sketch, "E214.MirrorCS", {"start": v(-707, 495.8) * mm, "end": v(-723, 495.8) * mm});
            skLineSegment(sketch, "E215.MirrorCS", {"start": v(-707, 604.2) * mm, "end": v(-707, 504.2) * mm, "construction": true});
            skPoint(sketch, "E216.MirrorP", {"position": v(-715, 600) * mm});
            skLineSegment(sketch, "E217", {"start": v(750, 750) * mm, "end": v(-750, -750) * mm, "construction": true});
            skArc(sketch, "E218.MirrorCS", {"start": v(723, -304.2) * mm, "mid": v(727.2, -300) * mm, "end": v(723, -295.8) * mm});
            skArc(sketch, "E219.MirrorCS", {"start": v(723, -4.2) * mm, "mid": v(727.2, 0) * mm, "end": v(723, 4.2) * mm});
            skLineSegment(sketch, "E220.MirrorCS", {"start": v(707, -4.2) * mm, "end": v(723, -4.2) * mm});
            skLineSegment(sketch, "E221.MirrorCS", {"start": v(723, 604.2) * mm, "end": v(723, 595.8) * mm, "construction": true});
            skArc(sketch, "E222.MirrorCS", {"start": v(707, 604.2) * mm, "mid": v(702.8, 600) * mm, "end": v(707, 595.8) * mm});
            skLineSegment(sketch, "E223.MirrorCS", {"start": v(707, 595.8) * mm, "end": v(723, 595.8) * mm});
            skArc(sketch, "E224.MirrorCS", {"start": v(723, 595.8) * mm, "mid": v(727.2, 600) * mm, "end": v(723, 604.2) * mm});
            skArc(sketch, "E225.MirrorCS", {"start": v(723, -104.2) * mm, "mid": v(727.2, -100) * mm, "end": v(723, -95.8) * mm});
            skArc(sketch, "E226.MirrorCS", {"start": v(707, 4.2) * mm, "mid": v(702.8, 0) * mm, "end": v(707, -4.2) * mm});
            skLineSegment(sketch, "E227.MirrorCS", {"start": v(707, 604.2) * mm, "end": v(723, 604.2) * mm});
            skLineSegment(sketch, "E228.MirrorCS", {"start": v(707, 4.2) * mm, "end": v(723, 4.2) * mm});
            skLineSegment(sketch, "E229.MirrorCS", {"start": v(707, 95.8) * mm, "end": v(723, 95.8) * mm});
            skLineSegment(sketch, "E230.MirrorCS", {"start": v(707, -204.2) * mm, "end": v(723, -204.2) * mm});
            skLineSegment(sketch, "E231.MirrorCS", {"start": v(707, -295.8) * mm, "end": v(723, -295.8) * mm});
            skLineSegment(sketch, "E232.MirrorCS", {"start": v(707, 304.2) * mm, "end": v(723, 304.2) * mm});
            skArc(sketch, "E233.MirrorCS", {"start": v(723, 95.8) * mm, "mid": v(727.2, 100) * mm, "end": v(723, 104.2) * mm});
            skLineSegment(sketch, "E234.MirrorCS", {"start": v(707, -395.8) * mm, "end": v(723, -395.8) * mm});
            skArc(sketch, "E235.MirrorCS", {"start": v(707, 104.2) * mm, "mid": v(702.8, 100) * mm, "end": v(707, 95.8) * mm});
            skArc(sketch, "E236.MirrorCS", {"start": v(707, 504.2) * mm, "mid": v(702.8, 500) * mm, "end": v(707, 495.8) * mm});
            skArc(sketch, "E237.MirrorCS", {"start": v(707, 204.2) * mm, "mid": v(702.8, 200) * mm, "end": v(707, 195.8) * mm});
            skLineSegment(sketch, "E238.MirrorCS", {"start": v(707, -104.2) * mm, "end": v(723, -104.2) * mm});
            skArc(sketch, "E239.MirrorCS", {"start": v(723, 395.8) * mm, "mid": v(727.2, 400) * mm, "end": v(723, 404.2) * mm});
            skArc(sketch, "E240.MirrorCS", {"start": v(723, 195.8) * mm, "mid": v(727.2, 200) * mm, "end": v(723, 204.2) * mm});
            skLineSegment(sketch, "E241.MirrorCS", {"start": v(707, 104.2) * mm, "end": v(723, 104.2) * mm});
            skArc(sketch, "E242.MirrorCS", {"start": v(707, -395.8) * mm, "mid": v(702.8, -400) * mm, "end": v(707, -404.2) * mm});
            skLineSegment(sketch, "E243.MirrorCS", {"start": v(707, -595.8) * mm, "end": v(723, -595.8) * mm});
            skArc(sketch, "E244.MirrorCS", {"start": v(723, -604.2) * mm, "mid": v(727.2, -600) * mm, "end": v(723, -595.8) * mm});
            skArc(sketch, "E245.MirrorCS", {"start": v(707, 304.2) * mm, "mid": v(702.8, 300) * mm, "end": v(707, 295.8) * mm});
            skArc(sketch, "E246.MirrorCS", {"start": v(723, -204.2) * mm, "mid": v(727.2, -200) * mm, "end": v(723, -195.8) * mm});
            skArc(sketch, "E247.MirrorCS", {"start": v(707, -195.8) * mm, "mid": v(702.8, -200) * mm, "end": v(707, -204.2) * mm});
            skLineSegment(sketch, "E248.MirrorCS", {"start": v(707, 204.2) * mm, "end": v(723, 204.2) * mm});
            skLineSegment(sketch, "E249.MirrorCS", {"start": v(707, -604.2) * mm, "end": v(723, -604.2) * mm});
            skLineSegment(sketch, "E250.MirrorCS", {"start": v(707, 395.8) * mm, "end": v(723, 395.8) * mm});
            skLineSegment(sketch, "E251.MirrorCS", {"start": v(707, -195.8) * mm, "end": v(723, -195.8) * mm});
            skLineSegment(sketch, "E252.MirrorCS", {"start": v(707, 295.8) * mm, "end": v(723, 295.8) * mm});
            skArc(sketch, "E253.MirrorCS", {"start": v(707, 404.2) * mm, "mid": v(702.8, 400) * mm, "end": v(707, 395.8) * mm});
            skLineSegment(sketch, "E254.MirrorCS", {"start": v(707, -304.2) * mm, "end": v(723, -304.2) * mm});
            skArc(sketch, "E255.MirrorCS", {"start": v(707, -95.8) * mm, "mid": v(702.8, -100) * mm, "end": v(707, -104.2) * mm});
            skArc(sketch, "E256.MirrorCS", {"start": v(723, -504.2) * mm, "mid": v(727.2, -500) * mm, "end": v(723, -495.8) * mm});
            skLineSegment(sketch, "E257.MirrorCS", {"start": v(707, 495.8) * mm, "end": v(723, 495.8) * mm});
            skArc(sketch, "E258.MirrorCS", {"start": v(707, -595.8) * mm, "mid": v(702.8, -600) * mm, "end": v(707, -604.2) * mm});
            skLineSegment(sketch, "E259.MirrorCS", {"start": v(707, 195.8) * mm, "end": v(723, 195.8) * mm});
            skLineSegment(sketch, "E260.MirrorCS", {"start": v(707, -95.8) * mm, "end": v(723, -95.8) * mm});
            skArc(sketch, "E261.MirrorCS", {"start": v(723, 495.8) * mm, "mid": v(727.2, 500) * mm, "end": v(723, 504.2) * mm});
            skLineSegment(sketch, "E262.MirrorCS", {"start": v(707, 404.2) * mm, "end": v(723, 404.2) * mm});
            skArc(sketch, "E263.MirrorCS", {"start": v(723, 295.8) * mm, "mid": v(727.2, 300) * mm, "end": v(723, 304.2) * mm});
            skLineSegment(sketch, "E264.MirrorCS", {"start": v(707, -495.8) * mm, "end": v(723, -495.8) * mm});
            skArc(sketch, "E265.MirrorCS", {"start": v(707, -495.8) * mm, "mid": v(702.8, -500) * mm, "end": v(707, -504.2) * mm});
            skLineSegment(sketch, "E266.MirrorCS", {"start": v(707, -404.2) * mm, "end": v(723, -404.2) * mm});
            skLineSegment(sketch, "E267.MirrorCS", {"start": v(707, -504.2) * mm, "end": v(723, -504.2) * mm});
            skArc(sketch, "E268.MirrorCS", {"start": v(723, -404.2) * mm, "mid": v(727.2, -400) * mm, "end": v(723, -395.8) * mm});
            skArc(sketch, "E269.MirrorCS", {"start": v(707, -295.8) * mm, "mid": v(702.8, -300) * mm, "end": v(707, -304.2) * mm});
            skLineSegment(sketch, "E270.MirrorCS", {"start": v(707, 504.2) * mm, "end": v(723, 504.2) * mm});
            skLineSegment(sketch, "E271.MirrorCS", {"start": v(-750, -750) * mm, "end": v(750, 750) * mm, "construction": true});
            skLineSegment(sketch, "E272.MirrorCS", {"start": v(707, 604.2) * mm, "end": v(707, 504.2) * mm, "construction": true});
            skPoint(sketch, "E273.MirrorP", {"position": v(715, 600) * mm});
            skCircle(sketch, "E274", {"center": v(-715, 715) * mm, "radius": 4.5 * mm});
            skCircle(sketch, "E275.MirrorC", {"center": v(715, 715) * mm, "radius": 4.5 * mm});
            skCircle(sketch, "E276.MirrorC", {"center": v(-715, -715) * mm, "radius": 4.5 * mm});
            skCircle(sketch, "E277.MirrorC", {"center": v(715, -715) * mm, "radius": 4.5 * mm});
            skLineSegment(sketch, "E278", {"start": v(-600, 715) * mm, "end": v(-750, 715) * mm, "construction": true});
            skSolve(sketch);
        }
        {
            var Q0;
            Q0 = qSketchRegion(id + "F6", true);
            extrude(context, id + "F7", {"entities" : qUnion([Q0]), "operationType" : NewBodyOperationType.REMOVE, "endBound" : BoundingType.THROUGH_ALL, "oppositeDirection" : true, "depth" : 25 * mm});
        }
        {
            var Q0;
            Q0=makeQuery(id+"F1.opExtrude","CAP_FACE",FACE,{"disambiguationData":[OSD([sQuery(id+"F0.wireOp",EDGE,"E0.bottom"),sQuery(id+"F0.wireOp",EDGE,"E0.top"),sQuery(id+"F0.wireOp",EDGE,"E0.left"),sQuery(id+"F0.wireOp",EDGE,"E0.right")])],"isStart":false});
            var sketch = newSketch(context, id + "F8", { "sketchPlane" : qUnion([Q0])});
            skCircle(sketch, "E279", {"center": v(311.8, 644.43) * mm, "radius": 4.5 * mm});
            skCircle(sketch, "E280", {"center": v(311.8, 544.43) * mm, "radius": 4.5 * mm});
            skCircle(sketch, "E281", {"center": v(345.55, 385.97) * mm, "radius": 4.5 * mm});
            skCircle(sketch, "E282", {"center": v(395.55, 299.37) * mm, "radius": 4.5 * mm});
            skLineSegment(sketch, "E283", {"start": v(311.8, 676.93) * mm, "end": v(311.8, 444.43) * mm, "construction": true});
            skLineSegment(sketch, "E284", {"start": v(311.8, 444.43) * mm, "end": v(479.3, 154.31) * mm, "construction": true});
            skLineSegment(sketch, "E285", {"start": v(395.55, 299.37) * mm, "end": v(242.04, 210.74) * mm, "construction": true});
            skCircle(sketch, "E286.MirrorC", {"center": v(445.55, 212.77) * mm, "radius": 4.5 * mm});
            skCircle(sketch, "E287.MirrorC", {"center": v(565.9, 104.31) * mm, "radius": 4.5 * mm});
            skCircle(sketch, "E288.MirrorC", {"center": v(652.5, 54.31) * mm, "radius": 4.5 * mm});
            skCircle(sketch, "E289", {"center": v(311.8, 494.43) * mm, "radius": 4.5 * mm});
            skCircle(sketch, "E290.MirrorC", {"center": v(522.6, 129.31) * mm, "radius": 4.5 * mm});
            skCircle(sketch, "E291", {"center": v(311.8, 594.43) * mm, "radius": 4.5 * mm});
            skCircle(sketch, "E292.MirrorC", {"center": v(609.2, 79.31) * mm, "radius": 4.5 * mm});
            skCircle(sketch, "E293", {"center": v(320.55, 429.27) * mm, "radius": 4.5 * mm});
            skLineSegment(sketch, "E294", {"start": v(0, 750) * mm, "end": v(0, -750) * mm, "construction": true});
            skPoint(sketch, "E295", {"position": v(311.8, 444.43) * mm});
            skLineSegment(sketch, "E296", {"start": v(127, 410) * mm, "end": v(357.07, 11.49) * mm, "construction": true});
            skPoint(sketch, "E297", {"position": v(242.04, 210.74) * mm});
            skLineSegment(sketch, "E298", {"start": v(218, 450.9) * mm, "end": v(438, 69.85) * mm, "construction": true});
            skLineSegment(sketch, "E299", {"start": v(218, 450.9) * mm, "end": v(0, 450.9) * mm, "construction": true});
            skLineSegment(sketch, "E300.MirrorCS", {"start": v(-218, 450.9) * mm, "end": v(0, 450.9) * mm, "construction": true});
            skLineSegment(sketch, "E301.MirrorCS", {"start": v(-218, 450.9) * mm, "end": v(-438, 69.85) * mm, "construction": true});
            skLineSegment(sketch, "E302", {"start": v(-328, 260.37) * mm, "end": v(-83.95, 119.47) * mm, "construction": true});
            skLineSegment(sketch, "E303.MirrorCS", {"start": v(-438, 69.85) * mm, "end": v(-329, -118.95) * mm, "construction": true});
            skLineSegment(sketch, "E304.MirrorCS", {"start": v(-220, -307.74) * mm, "end": v(-329, -118.95) * mm, "construction": true});
            skLineSegment(sketch, "E305", {"start": v(328, 260.37) * mm, "end": v(242.04, 210.74) * mm, "construction": true});
            skLineSegment(sketch, "E306.MirrorCS", {"start": v(438, 69.85) * mm, "end": v(329, -118.95) * mm, "construction": true});
            skLineSegment(sketch, "E307.MirrorCS", {"start": v(220, -307.74) * mm, "end": v(329, -118.95) * mm, "construction": true});
            skLineSegment(sketch, "E308.MirrorCS", {"start": v(220, -307.74) * mm, "end": v(-220, -307.74) * mm, "construction": true});
            skCircle(sketch, "E309.MirrorC", {"center": v(-522.6, 129.31) * mm, "radius": 4.5 * mm});
            skCircle(sketch, "E310.MirrorC", {"center": v(-565.9, 104.31) * mm, "radius": 4.5 * mm});
            skCircle(sketch, "E311.MirrorC", {"center": v(-609.2, 79.31) * mm, "radius": 4.5 * mm});
            skCircle(sketch, "E312.MirrorC", {"center": v(-652.5, 54.31) * mm, "radius": 4.5 * mm});
            skCircle(sketch, "E313.MirrorC", {"center": v(-311.8, 544.43) * mm, "radius": 4.5 * mm});
            skCircle(sketch, "E314.MirrorC", {"center": v(-311.8, 594.43) * mm, "radius": 4.5 * mm});
            skCircle(sketch, "E315.MirrorC", {"center": v(-311.8, 644.43) * mm, "radius": 4.5 * mm});
            skCircle(sketch, "E316.MirrorC", {"center": v(-311.8, 494.43) * mm, "radius": 4.5 * mm});
            skCircle(sketch, "E317.MirrorC", {"center": v(-320.55, 429.27) * mm, "radius": 4.5 * mm});
            skCircle(sketch, "E318.MirrorC", {"center": v(-345.55, 385.97) * mm, "radius": 4.5 * mm});
            skCircle(sketch, "E319.MirrorC", {"center": v(-395.55, 299.37) * mm, "radius": 4.5 * mm});
            skCircle(sketch, "E320.MirrorC", {"center": v(-445.55, 212.77) * mm, "radius": 4.5 * mm});
            skCircle(sketch, "E321.MirrorC", {"center": v(210.8, -410.74) * mm, "radius": 4.5 * mm});
            skCircle(sketch, "E322.MirrorC", {"center": v(297.4, -460.74) * mm, "radius": 4.5 * mm});
            skCircle(sketch, "E323.MirrorC", {"center": v(340.7, -485.74) * mm, "radius": 4.5 * mm});
            skCircle(sketch, "E324.MirrorC", {"center": v(254.1, -435.74) * mm, "radius": 4.5 * mm});
            skCircle(sketch, "E325.MirrorC", {"center": v(100, -385.74) * mm, "radius": 4.5 * mm});
            skLineSegment(sketch, "E326.MirrorCS", {"start": v(-220, -307.74) * mm, "end": v(220, -307.74) * mm, "construction": true});
            skCircle(sketch, "E327.MirrorC", {"center": v(-150, -385.74) * mm, "radius": 4.5 * mm});
            skCircle(sketch, "E328.MirrorC", {"center": v(0, -385.74) * mm, "radius": 4.5 * mm});
            skCircle(sketch, "E329.MirrorC", {"center": v(-297.4, -460.74) * mm, "radius": 4.5 * mm});
            skCircle(sketch, "E330.MirrorC", {"center": v(-340.7, -485.74) * mm, "radius": 4.5 * mm});
            skCircle(sketch, "E331.MirrorC", {"center": v(-210.8, -410.74) * mm, "radius": 4.5 * mm});
            skCircle(sketch, "E332.MirrorC", {"center": v(-254.1, -435.74) * mm, "radius": 4.5 * mm});
            skCircle(sketch, "E333.MirrorC", {"center": v(-100, -385.74) * mm, "radius": 4.5 * mm});
            skCircle(sketch, "E334.MirrorC", {"center": v(470.55, 169.47) * mm, "radius": 4.5 * mm});
            skCircle(sketch, "E335.MirrorC", {"center": v(150, -385.74) * mm, "radius": 4.5 * mm});
            skCircle(sketch, "E336.MirrorC", {"center": v(-470.55, 169.47) * mm, "radius": 4.5 * mm});
            skCircle(sketch, "E337", {"center": v(-650.82, -131.54) * mm, "radius": 4.5 * mm});
            skCircle(sketch, "E338.1.0.0", {"center": v(-600.82, -218.15) * mm, "radius": 4.5 * mm});
            skCircle(sketch, "E338.2.0.0", {"center": v(-550.82, -304.75) * mm, "radius": 4.5 * mm});
            skCircle(sketch, "E338.3.0.0", {"center": v(-500.82, -391.35) * mm, "radius": 4.5 * mm});
            skCircle(sketch, "E338.4.0.0", {"center": v(-450.82, -477.95) * mm, "radius": 4.5 * mm});
            skLineSegment(sketch, "E338.direction1", {"start": v(-650.82, -131.54) * mm, "end": v(-600.82, -218.15) * mm, "construction": true});
            skCircle(sketch, "E339.0.5.0", {"center": v(-400.82, -564.56) * mm, "radius": 4.5 * mm});
            skCircle(sketch, "E339.0.6.0", {"center": v(-350.82, -651.16) * mm, "radius": 4.5 * mm});
            skLineSegment(sketch, "E340", {"start": v(750, 750) * mm, "end": v(-750, -750) * mm, "construction": true});
            skCircle(sketch, "E341", {"center": v(691.42, 691.42) * mm, "radius": 4.5 * mm});
            skCircle(sketch, "E342.1.0.0", {"center": v(620.71, 620.71) * mm, "radius": 4.5 * mm});
            skCircle(sketch, "E342.2.0.0", {"center": v(550, 550) * mm, "radius": 4.5 * mm});
            skCircle(sketch, "E342.3.0.0", {"center": v(479.29, 479.29) * mm, "radius": 4.5 * mm});
            skCircle(sketch, "E342.4.0.0", {"center": v(408.58, 408.58) * mm, "radius": 4.5 * mm});
            skLineSegment(sketch, "E342.direction1", {"start": v(691.42, 691.42) * mm, "end": v(620.71, 620.71) * mm, "construction": true});
            skCircle(sketch, "E343.MirrorC", {"center": v(-408.58, 408.58) * mm, "radius": 4.5 * mm});
            skCircle(sketch, "E344.MirrorC", {"center": v(-550, 550) * mm, "radius": 4.5 * mm});
            skCircle(sketch, "E345.MirrorC", {"center": v(-479.29, 479.29) * mm, "radius": 4.5 * mm});
            skCircle(sketch, "E346.MirrorC", {"center": v(-620.71, 620.71) * mm, "radius": 4.5 * mm});
            skCircle(sketch, "E347.MirrorC", {"center": v(-691.42, 691.42) * mm, "radius": 4.5 * mm});
            skLineSegment(sketch, "E348", {"start": v(-484.1, -208.5) * mm, "end": v(-575.82, -261.45) * mm, "construction": true});
            skLineSegment(sketch, "E349", {"start": v(-600.82, -218.15) * mm, "end": v(-550.82, -304.75) * mm, "construction": true});
            skCircle(sketch, "E350.MirrorC", {"center": v(600.82, -218.15) * mm, "radius": 4.5 * mm});
            skCircle(sketch, "E351.MirrorC", {"center": v(550.82, -304.75) * mm, "radius": 4.5 * mm});
            skCircle(sketch, "E352.MirrorC", {"center": v(650.82, -131.54) * mm, "radius": 4.5 * mm});
            skCircle(sketch, "E353.MirrorC", {"center": v(450.82, -477.95) * mm, "radius": 4.5 * mm});
            skCircle(sketch, "E354.MirrorC", {"center": v(500.82, -391.35) * mm, "radius": 4.5 * mm});
            skCircle(sketch, "E355.MirrorC", {"center": v(400.82, -564.56) * mm, "radius": 4.5 * mm});
            skCircle(sketch, "E356.MirrorC", {"center": v(350.82, -651.16) * mm, "radius": 4.5 * mm});
            skCircle(sketch, "E357", {"center": v(0, 0) * mm, "radius": 4.5 * mm});
            skCircle(sketch, "E358.0.1.0", {"center": v(-70.71, 70.71) * mm, "radius": 4.5 * mm});
            skCircle(sketch, "E358.0.2.0", {"center": v(-141.42, 141.42) * mm, "radius": 4.5 * mm});
            skCircle(sketch, "E358.0.3.0", {"center": v(-212.13, 212.13) * mm, "radius": 4.5 * mm});
            skCircle(sketch, "E358.0.4.0", {"center": v(-282.84, 282.84) * mm, "radius": 4.5 * mm});
            skLineSegment(sketch, "E358.direction1", {"start": v(0, 0) * mm, "end": v(38.96, 38.96) * mm, "construction": true});
            skLineSegment(sketch, "E358.direction2", {"start": v(0, 0) * mm, "end": v(-70.71, 70.71) * mm, "construction": true});
            skCircle(sketch, "E359.1.0.0", {"center": v(70.71, 70.71) * mm, "radius": 4.5 * mm});
            skCircle(sketch, "E359.2.0.0", {"center": v(141.42, 141.42) * mm, "radius": 4.5 * mm});
            skCircle(sketch, "E359.3.0.0", {"center": v(212.13, 212.13) * mm, "radius": 4.5 * mm});
            skCircle(sketch, "E359.4.0.0", {"center": v(282.84, 282.84) * mm, "radius": 4.5 * mm});
            skLineSegment(sketch, "E359.direction1", {"start": v(0, 0) * mm, "end": v(70.71, 70.71) * mm, "construction": true});
            skCircle(sketch, "E360.1.0.0", {"center": v(-70.71, -70.71) * mm, "radius": 4.5 * mm});
            skCircle(sketch, "E360.2.0.0", {"center": v(-141.42, -141.42) * mm, "radius": 4.5 * mm});
            skLineSegment(sketch, "E360.direction1", {"start": v(0, 0) * mm, "end": v(-70.71, -70.71) * mm, "construction": true});
            skCircle(sketch, "E361.1.0.0", {"center": v(70.71, -70.71) * mm, "radius": 4.5 * mm});
            skCircle(sketch, "E361.2.0.0", {"center": v(141.42, -141.42) * mm, "radius": 4.5 * mm});
            skLineSegment(sketch, "E361.direction1", {"start": v(0, 0) * mm, "end": v(70.71, -70.71) * mm, "construction": true});
            skSolve(sketch);
        }
        {
            var Q0;
            Q0 = qSketchRegion(id + "F8", true);
            extrude(context, id + "F9", {"entities" : qUnion([Q0]), "operationType" : NewBodyOperationType.REMOVE, "endBound" : BoundingType.THROUGH_ALL, "oppositeDirection" : true, "depth" : 25 * mm});
        }
        {
            var Q0;
            Q0=makeQuery(id+"F1.opExtrude","SWEPT_EDGE",EDGE,{"disambiguationData":[OSD([sQuery(id+"F0.wireOp",EDGE,"E0.top"),sQuery(id+"F0.wireOp",EDGE,"E0.right")])]});
            var Q1;
            Q1=makeQuery(id+"F1.opExtrude","SWEPT_EDGE",EDGE,{"disambiguationData":[OSD([sQuery(id+"F0.wireOp",EDGE,"E0.top"),sQuery(id+"F0.wireOp",EDGE,"E0.left")])]});
            var Q2;
            Q2=makeQuery(id+"F1.opExtrude","SWEPT_EDGE",EDGE,{"disambiguationData":[OSD([sQuery(id+"F0.wireOp",EDGE,"E0.bottom"),sQuery(id+"F0.wireOp",EDGE,"E0.left")])]});
            var Q3;
            Q3=makeQuery(id+"F1.opExtrude","SWEPT_EDGE",EDGE,{"disambiguationData":[OSD([sQuery(id+"F0.wireOp",EDGE,"E0.bottom"),sQuery(id+"F0.wireOp",EDGE,"E0.right")])]});
            fillet(context, id + "F10", {"entities" : qUnion([Q0, Q1, Q2, Q3]), "radius" : 10 * mm, "tangentPropagation" : true, "allowEdgeOverflow" : false});
        }
        {
            var Q0;
            Q0=makeQuery(id+"F5.boolean.opBoolean","COPY",EDGE,{"derivedFrom":makeQuery(id+"F5.opExtrude","SWEPT_EDGE",EDGE,{"disambiguationData":[OSD([sQuery(id+"F4.wireOp",EDGE,"E27"),sQuery(id+"F4.wireOp",EDGE,"E28")])]})});
            var Q1;
            Q1=makeQuery(id+"F5.boolean.opBoolean","COPY",EDGE,{"derivedFrom":makeQuery(id+"F5.opExtrude","SWEPT_EDGE",EDGE,{"disambiguationData":[OSD([sQuery(id+"F4.wireOp",EDGE,"E27"),sQuery(id+"F4.wireOp",EDGE,"E96.MirrorCS")])]})});
            var Q2;
            Q2=makeQuery(id+"F5.boolean.opBoolean","COPY",EDGE,{"derivedFrom":makeQuery(id+"F5.opExtrude","SWEPT_EDGE",EDGE,{"disambiguationData":[OSD([sQuery(id+"F4.wireOp",EDGE,"E28"),sQuery(id+"F4.wireOp",EDGE,"E97.MirrorCS")])]})});
            var Q3;
            Q3=makeQuery(id+"F5.boolean.opBoolean","COPY",EDGE,{"derivedFrom":makeQuery(id+"F5.opExtrude","SWEPT_EDGE",EDGE,{"disambiguationData":[OSD([sQuery(id+"F4.wireOp",EDGE,"E29.MirrorCS"),sQuery(id+"F4.wireOp",EDGE,"E30.MirrorCS")])]})});
            var Q4;
            Q4=makeQuery(id+"F5.boolean.opBoolean","COPY",EDGE,{"derivedFrom":makeQuery(id+"F5.opExtrude","SWEPT_EDGE",EDGE,{"disambiguationData":[OSD([sQuery(id+"F4.wireOp",EDGE,"E29.MirrorCS"),sQuery(id+"F4.wireOp",EDGE,"E95")])]})});
            var Q5;
            Q5=makeQuery(id+"F5.boolean.opBoolean","COPY",EDGE,{"derivedFrom":makeQuery(id+"F5.opExtrude","SWEPT_EDGE",EDGE,{"disambiguationData":[OSD([sQuery(id+"F4.wireOp",EDGE,"E30.MirrorCS"),sQuery(id+"F4.wireOp",EDGE,"E94")])]})});
            var Q6;
            Q6=makeQuery(id+"F5.boolean.opBoolean","COPY",EDGE,{"derivedFrom":makeQuery(id+"F5.opExtrude","SWEPT_EDGE",EDGE,{"disambiguationData":[OSD([sQuery(id+"F4.wireOp",EDGE,"E67.MirrorCS"),sQuery(id+"F4.wireOp",EDGE,"E68.MirrorCS")])]})});
            var Q7;
            Q7=makeQuery(id+"F5.boolean.opBoolean","COPY",EDGE,{"derivedFrom":makeQuery(id+"F5.opExtrude","SWEPT_EDGE",EDGE,{"disambiguationData":[OSD([sQuery(id+"F4.wireOp",EDGE,"E68.MirrorCS"),sQuery(id+"F4.wireOp",EDGE,"E71.MirrorCS")])]})});
            var Q8;
            Q8=makeQuery(id+"F5.boolean.opBoolean","COPY",EDGE,{"derivedFrom":makeQuery(id+"F5.opExtrude","SWEPT_EDGE",EDGE,{"disambiguationData":[OSD([sQuery(id+"F4.wireOp",EDGE,"E71.MirrorCS"),sQuery(id+"F4.wireOp",EDGE,"E72.MirrorCS")])]})});
            var Q9;
            Q9=makeQuery(id+"F5.boolean.opBoolean","COPY",EDGE,{"derivedFrom":makeQuery(id+"F5.opExtrude","SWEPT_EDGE",EDGE,{"disambiguationData":[OSD([sQuery(id+"F4.wireOp",EDGE,"E67.MirrorCS"),sQuery(id+"F4.wireOp",EDGE,"E72.MirrorCS")])]})});
            var Q10;
            Q10=makeQuery(id+"F5.boolean.opBoolean","COPY",EDGE,{"derivedFrom":makeQuery(id+"F5.opExtrude","SWEPT_EDGE",EDGE,{"disambiguationData":[OSD([sQuery(id+"F4.wireOp",EDGE,"E50"),sQuery(id+"F4.wireOp",EDGE,"E51")])]})});
            var Q11;
            Q11=makeQuery(id+"F5.boolean.opBoolean","COPY",EDGE,{"derivedFrom":makeQuery(id+"F5.opExtrude","SWEPT_EDGE",EDGE,{"disambiguationData":[OSD([sQuery(id+"F4.wireOp",EDGE,"E50"),sQuery(id+"F4.wireOp",EDGE,"E69")])]})});
            var Q12;
            Q12=makeQuery(id+"F5.boolean.opBoolean","COPY",EDGE,{"derivedFrom":makeQuery(id+"F5.opExtrude","SWEPT_EDGE",EDGE,{"disambiguationData":[OSD([sQuery(id+"F4.wireOp",EDGE,"E69"),sQuery(id+"F4.wireOp",EDGE,"E70")])]})});
            var Q13;
            Q13=makeQuery(id+"F5.boolean.opBoolean","COPY",EDGE,{"derivedFrom":makeQuery(id+"F5.opExtrude","SWEPT_EDGE",EDGE,{"disambiguationData":[OSD([sQuery(id+"F4.wireOp",EDGE,"E51"),sQuery(id+"F4.wireOp",EDGE,"E70")])]})});
            var Q14;
            Q14=makeQuery(id+"F5.boolean.opBoolean","COPY",EDGE,{"derivedFrom":makeQuery(id+"F5.opExtrude","SWEPT_EDGE",EDGE,{"disambiguationData":[OSD([sQuery(id+"F4.wireOp",EDGE,"E85"),sQuery(id+"F4.wireOp",EDGE,"E86")])]})});
            var Q15;
            Q15=makeQuery(id+"F5.boolean.opBoolean","COPY",EDGE,{"derivedFrom":makeQuery(id+"F5.opExtrude","SWEPT_EDGE",EDGE,{"disambiguationData":[OSD([sQuery(id+"F4.wireOp",EDGE,"E87.MirrorCS"),sQuery(id+"F4.wireOp",EDGE,"E88.MirrorCS")])]})});
            var Q16;
            Q16=makeQuery(id+"F5.boolean.opBoolean","COPY",EDGE,{"derivedFrom":makeQuery(id+"F5.opExtrude","SWEPT_EDGE",EDGE,{"disambiguationData":[OSD([sQuery(id+"F4.wireOp",EDGE,"E32"),sQuery(id+"F4.wireOp",EDGE,"E88.MirrorCS")])]})});
            var Q17;
            Q17=makeQuery(id+"F5.boolean.opBoolean","COPY",EDGE,{"derivedFrom":makeQuery(id+"F5.opExtrude","SWEPT_EDGE",EDGE,{"disambiguationData":[OSD([sQuery(id+"F4.wireOp",EDGE,"E32"),sQuery(id+"F4.wireOp",EDGE,"E33.MirrorCS")])]})});
            var Q18;
            Q18=makeQuery(id+"F5.boolean.opBoolean","COPY",EDGE,{"derivedFrom":makeQuery(id+"F5.opExtrude","SWEPT_EDGE",EDGE,{"disambiguationData":[OSD([sQuery(id+"F4.wireOp",EDGE,"E33.MirrorCS"),sQuery(id+"F4.wireOp",EDGE,"E85")])]})});
            var Q19;
            Q19=makeQuery(id+"F5.boolean.opBoolean","COPY",EDGE,{"derivedFrom":makeQuery(id+"F5.opExtrude","SWEPT_EDGE",EDGE,{"disambiguationData":[OSD([sQuery(id+"F4.wireOp",EDGE,"E78"),sQuery(id+"F4.wireOp",EDGE,"E79")])]})});
            var Q20;
            Q20=makeQuery(id+"F5.boolean.opBoolean","COPY",EDGE,{"derivedFrom":makeQuery(id+"F5.opExtrude","SWEPT_EDGE",EDGE,{"disambiguationData":[OSD([sQuery(id+"F4.wireOp",EDGE,"E79"),sQuery(id+"F4.wireOp",EDGE,"E80")])]})});
            var Q21;
            Q21=makeQuery(id+"F5.boolean.opBoolean","COPY",EDGE,{"derivedFrom":makeQuery(id+"F5.opExtrude","SWEPT_EDGE",EDGE,{"disambiguationData":[OSD([sQuery(id+"F4.wireOp",EDGE,"E38"),sQuery(id+"F4.wireOp",EDGE,"E39.MirrorCS")])]})});
            var Q22;
            Q22=makeQuery(id+"F5.boolean.opBoolean","COPY",EDGE,{"derivedFrom":makeQuery(id+"F5.opExtrude","SWEPT_EDGE",EDGE,{"disambiguationData":[OSD([sQuery(id+"F4.wireOp",EDGE,"E38"),sQuery(id+"F4.wireOp",EDGE,"E47")])]})});
            var Q23;
            Q23=makeQuery(id+"F5.boolean.opBoolean","COPY",EDGE,{"derivedFrom":makeQuery(id+"F5.opExtrude","SWEPT_EDGE",EDGE,{"disambiguationData":[OSD([sQuery(id+"F4.wireOp",EDGE,"E81.MirrorCS"),sQuery(id+"F4.wireOp",EDGE,"E83.MirrorCS")])]})});
            var Q24;
            Q24=makeQuery(id+"F5.boolean.opBoolean","COPY",EDGE,{"derivedFrom":makeQuery(id+"F5.opExtrude","SWEPT_EDGE",EDGE,{"disambiguationData":[OSD([sQuery(id+"F4.wireOp",EDGE,"E81.MirrorCS"),sQuery(id+"F4.wireOp",EDGE,"E82.MirrorCS")])]})});
            var Q25;
            Q25=makeQuery(id+"F5.boolean.opBoolean","COPY",EDGE,{"derivedFrom":makeQuery(id+"F5.opExtrude","SWEPT_EDGE",EDGE,{"disambiguationData":[OSD([sQuery(id+"F4.wireOp",EDGE,"E41.MirrorCS"),sQuery(id+"F4.wireOp",EDGE,"E48.MirrorCS")])]})});
            var Q26;
            Q26=makeQuery(id+"F5.boolean.opBoolean","COPY",EDGE,{"derivedFrom":makeQuery(id+"F5.opExtrude","SWEPT_EDGE",EDGE,{"disambiguationData":[OSD([sQuery(id+"F4.wireOp",EDGE,"E40.MirrorCS"),sQuery(id+"F4.wireOp",EDGE,"E41.MirrorCS")])]})});
            var Q27;
            Q27=makeQuery(id+"F5.boolean.opBoolean","COPY",EDGE,{"derivedFrom":makeQuery(id+"F5.opExtrude","SWEPT_EDGE",EDGE,{"disambiguationData":[OSD([sQuery(id+"F4.wireOp",EDGE,"E35.MirrorCS"),sQuery(id+"F4.wireOp",EDGE,"E37.MirrorCS")])]})});
            var Q28;
            Q28=makeQuery(id+"F5.boolean.opBoolean","COPY",EDGE,{"derivedFrom":makeQuery(id+"F5.opExtrude","SWEPT_EDGE",EDGE,{"disambiguationData":[OSD([sQuery(id+"F4.wireOp",EDGE,"E37.MirrorCS"),sQuery(id+"F4.wireOp",EDGE,"E76.MirrorCS")])]})});
            var Q29;
            Q29=makeQuery(id+"F5.boolean.opBoolean","COPY",EDGE,{"derivedFrom":makeQuery(id+"F5.opExtrude","SWEPT_EDGE",EDGE,{"disambiguationData":[OSD([sQuery(id+"F4.wireOp",EDGE,"E75.MirrorCS"),sQuery(id+"F4.wireOp",EDGE,"E76.MirrorCS")])]})});
            var Q30;
            Q30=makeQuery(id+"F5.boolean.opBoolean","COPY",EDGE,{"derivedFrom":makeQuery(id+"F5.opExtrude","SWEPT_EDGE",EDGE,{"disambiguationData":[OSD([sQuery(id+"F4.wireOp",EDGE,"E73"),sQuery(id+"F4.wireOp",EDGE,"E74")])]})});
            var Q31;
            Q31=makeQuery(id+"F5.boolean.opBoolean","COPY",EDGE,{"derivedFrom":makeQuery(id+"F5.opExtrude","SWEPT_EDGE",EDGE,{"disambiguationData":[OSD([sQuery(id+"F4.wireOp",EDGE,"E35.MirrorCS"),sQuery(id+"F4.wireOp",EDGE,"E73")])]})});
            var Q32;
            Q32=makeQuery(id+"F5.boolean.opBoolean","COPY",EDGE,{"derivedFrom":makeQuery(id+"F5.opExtrude","SWEPT_EDGE",EDGE,{"disambiguationData":[OSD([sQuery(id+"F4.wireOp",EDGE,"E56"),sQuery(id+"F4.wireOp",EDGE,"E57")])]})});
            var Q33;
            Q33=makeQuery(id+"F5.boolean.opBoolean","COPY",EDGE,{"derivedFrom":makeQuery(id+"F5.opExtrude","SWEPT_EDGE",EDGE,{"disambiguationData":[OSD([sQuery(id+"F4.wireOp",EDGE,"E61"),sQuery(id+"F4.wireOp",EDGE,"E62")])]})});
            var Q34;
            Q34=makeQuery(id+"F5.boolean.opBoolean","COPY",EDGE,{"derivedFrom":makeQuery(id+"F5.opExtrude","SWEPT_EDGE",EDGE,{"disambiguationData":[OSD([sQuery(id+"F4.wireOp",EDGE,"E64.MirrorCS"),sQuery(id+"F4.wireOp",EDGE,"E66.MirrorCS")])]})});
            var Q35;
            Q35=makeQuery(id+"F5.boolean.opBoolean","COPY",EDGE,{"derivedFrom":makeQuery(id+"F5.opExtrude","SWEPT_EDGE",EDGE,{"disambiguationData":[OSD([sQuery(id+"F4.wireOp",EDGE,"E66.MirrorCS"),sQuery(id+"F4.wireOp",EDGE,"E92.MirrorCS")])]})});
            var Q36;
            Q36=makeQuery(id+"F5.boolean.opBoolean","COPY",EDGE,{"derivedFrom":makeQuery(id+"F5.opExtrude","SWEPT_EDGE",EDGE,{"disambiguationData":[OSD([sQuery(id+"F4.wireOp",EDGE,"E91.MirrorCS"),sQuery(id+"F4.wireOp",EDGE,"E92.MirrorCS")])]})});
            var Q37;
            Q37=makeQuery(id+"F5.boolean.opBoolean","COPY",EDGE,{"derivedFrom":makeQuery(id+"F5.opExtrude","SWEPT_EDGE",EDGE,{"disambiguationData":[OSD([sQuery(id+"F4.wireOp",EDGE,"E89"),sQuery(id+"F4.wireOp",EDGE,"E90")])]})});
            var Q38;
            Q38=makeQuery(id+"F5.boolean.opBoolean","COPY",EDGE,{"derivedFrom":makeQuery(id+"F5.opExtrude","SWEPT_EDGE",EDGE,{"disambiguationData":[OSD([sQuery(id+"F4.wireOp",EDGE,"E62"),sQuery(id+"F4.wireOp",EDGE,"E89")])]})});
            var Q39;
            Q39=makeQuery(id+"F5.boolean.opBoolean","COPY",EDGE,{"derivedFrom":makeQuery(id+"F5.opExtrude","SWEPT_EDGE",EDGE,{"disambiguationData":[OSD([sQuery(id+"F4.wireOp",EDGE,"E58.MirrorCS"),sQuery(id+"F4.wireOp",EDGE,"E59.MirrorCS")])]})});
            fillet(context, id + "F11", {"entities" : qUnion([Q0, Q1, Q2, Q3, Q4, Q5, Q6, Q7, Q8, Q9, Q10, Q11, Q12, Q13, Q14, Q15, Q16, Q17, Q18, Q19, Q20, Q21, Q22, Q23, Q24, Q25, Q26, Q27, Q28, Q29, Q30, Q31, Q32, Q33, Q34, Q35, Q36, Q37, Q38, Q39]), "radius" : 20 * mm, "tangentPropagation" : true, "allowEdgeOverflow" : false});
        }
        {
            var Q0;
            Q0=makeQuery(id+"F5.boolean.opBoolean","COPY",EDGE,{"derivedFrom":makeQuery(id+"F5.opExtrude","SWEPT_EDGE",EDGE,{"disambiguationData":[OSD([sQuery(id+"F4.wireOp",EDGE,"E55"),sQuery(id+"F4.wireOp",EDGE,"E57")])]})});
            var Q1;
            Q1=makeQuery(id+"F5.boolean.opBoolean","COPY",EDGE,{"derivedFrom":makeQuery(id+"F5.opExtrude","SWEPT_EDGE",EDGE,{"disambiguationData":[OSD([sQuery(id+"F4.wireOp",EDGE,"E55"),sQuery(id+"F4.wireOp",EDGE,"E56")])]})});
            var Q2;
            Q2=makeQuery(id+"F5.boolean.opBoolean","COPY",EDGE,{"derivedFrom":makeQuery(id+"F5.opExtrude","SWEPT_EDGE",EDGE,{"disambiguationData":[OSD([sQuery(id+"F4.wireOp",EDGE,"E58.MirrorCS"),sQuery(id+"F4.wireOp",EDGE,"E60.MirrorCS")])]})});
            var Q3;
            Q3=makeQuery(id+"F5.boolean.opBoolean","COPY",EDGE,{"derivedFrom":makeQuery(id+"F5.opExtrude","SWEPT_EDGE",EDGE,{"disambiguationData":[OSD([sQuery(id+"F4.wireOp",EDGE,"E59.MirrorCS"),sQuery(id+"F4.wireOp",EDGE,"E60.MirrorCS")])]})});
            fillet(context, id + "F12", {"entities" : qUnion([Q0, Q1, Q2, Q3]), "radius" : 10 * mm, "tangentPropagation" : true, "allowEdgeOverflow" : false});
        }
        {
            var Q0;
            Q0=makeQuery(id+"F5.boolean.opBoolean","COPY",EDGE,{"derivedFrom":makeQuery(id+"F5.opExtrude","SWEPT_EDGE",EDGE,{"disambiguationData":[OSD([sQuery(id+"F4.wireOp",EDGE,"E96.MirrorCS"),sQuery(id+"F4.wireOp",EDGE,"E97.MirrorCS")])]})});
            var Q1;
            Q1=makeQuery(id+"F5.boolean.opBoolean","COPY",EDGE,{"derivedFrom":makeQuery(id+"F5.opExtrude","SWEPT_EDGE",EDGE,{"disambiguationData":[OSD([sQuery(id+"F4.wireOp",EDGE,"E94"),sQuery(id+"F4.wireOp",EDGE,"E95")])]})});
            fillet(context, id + "F13", {"entities" : qUnion([Q0, Q1]), "radius" : 50 * mm, "tangentPropagation" : true, "allowEdgeOverflow" : false});
        }
        {
            var Q0;
            Q0=makeQuery(id+"F1.opExtrude","CAP_FACE",FACE,{"disambiguationData":[OSD([sQuery(id+"F0.wireOp",EDGE,"E0.bottom"),sQuery(id+"F0.wireOp",EDGE,"E0.top"),sQuery(id+"F0.wireOp",EDGE,"E0.left"),sQuery(id+"F0.wireOp",EDGE,"E0.right")])],"isStart":false});
            var sketch = newSketch(context, id + "F14", { "sketchPlane" : qUnion([Q0])});
            skLineSegment(sketch, "E362", {"start": v(0, 750) * mm, "end": v(0, 550.88) * mm, "construction": true});
            skLineSegment(sketch, "E363", {"start": v(-79.13, 750) * mm, "end": v(-750, -411.97) * mm, "construction": true});
            skCircle(sketch, "E364", {"center": v(-235, 480.03) * mm, "radius": 4.1 * mm});
            skCircle(sketch, "E365.1.0.0", {"center": v(-285, 393.43) * mm, "radius": 4.1 * mm});
            skCircle(sketch, "E365.2.0.0", {"center": v(-335, 306.83) * mm, "radius": 4.1 * mm});
            skLineSegment(sketch, "E365.direction1", {"start": v(-235, 480.03) * mm, "end": v(-285, 393.43) * mm, "construction": true});
            skCircle(sketch, "E366.MirrorC", {"center": v(335, 306.83) * mm, "radius": 4.1 * mm});
            skCircle(sketch, "E367.MirrorC", {"center": v(285, 393.43) * mm, "radius": 4.1 * mm});
            skCircle(sketch, "E368.MirrorC", {"center": v(235, 480.03) * mm, "radius": 4.1 * mm});
            skCircle(sketch, "E369.0.3.0", {"center": v(-385, 220.22) * mm, "radius": 4.1 * mm});
            skCircle(sketch, "E370.MirrorC", {"center": v(385, 220.22) * mm, "radius": 4.1 * mm});
            skPoint(sketch, "E371", {"position": v(-92, 470.03) * mm});
            skCircle(sketch, "E372.0.4.0", {"center": v(-435, 133.62) * mm, "radius": 4.1 * mm});
            skCircle(sketch, "E373.MirrorC", {"center": v(435, 133.62) * mm, "radius": 4.1 * mm});
            skCircle(sketch, "E374.0.5.0", {"center": v(-485, 47.02) * mm, "radius": 4.1 * mm});
            skCircle(sketch, "E375.MirrorC", {"center": v(485, 47.02) * mm, "radius": 4.1 * mm});
            skSolve(sketch);
        }
        {
            var Q0;
            Q0 = qSketchRegion(id + "F14", true);
            extrude(context, id + "F15", {"entities" : qUnion([Q0]), "operationType" : NewBodyOperationType.REMOVE, "endBound" : BoundingType.THROUGH_ALL, "oppositeDirection" : true, "depth" : 25 * mm});
        }
    });
